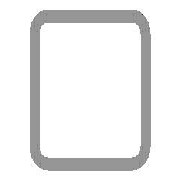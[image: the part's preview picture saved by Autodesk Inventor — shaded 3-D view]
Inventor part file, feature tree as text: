
AUTODESK INVENTOR PART (.ipt)
format: ipt  version: 2024.2 (Build 282272000, 272)  size: 129,024 bytes
history: native  units: mm (DEFAULTED — no unit token found)
features: other x4, sketch x1, plane x1
ambient origin geometry x8: Origin, YZ Plane, XZ Plane, XY Plane, X Axis, Y Axis, Z Axis, Center Point
bodies: Solid1 (feature_tree), Body (feature_tree)
feature tree (6):
  parser-record x1  (decoder bookkeeping rows leaked as tree rows — omitted from the tree; the rows remain in map.json)
  other  "Driven Length"
  other  "Start Plane"
  other  "End Plane"
  sketch  "Sketch3"  dims[d3=700.0mm d4=0.0mm d7=4.0mm d9=40.0mm d11=40.0mm d12=2.0mm d13=-0.0mm d14=700.0mm d15=20.0mm d16=20.0mm d17=90.0deg d18=700.0mm]
  plane  "Work Plane3"
